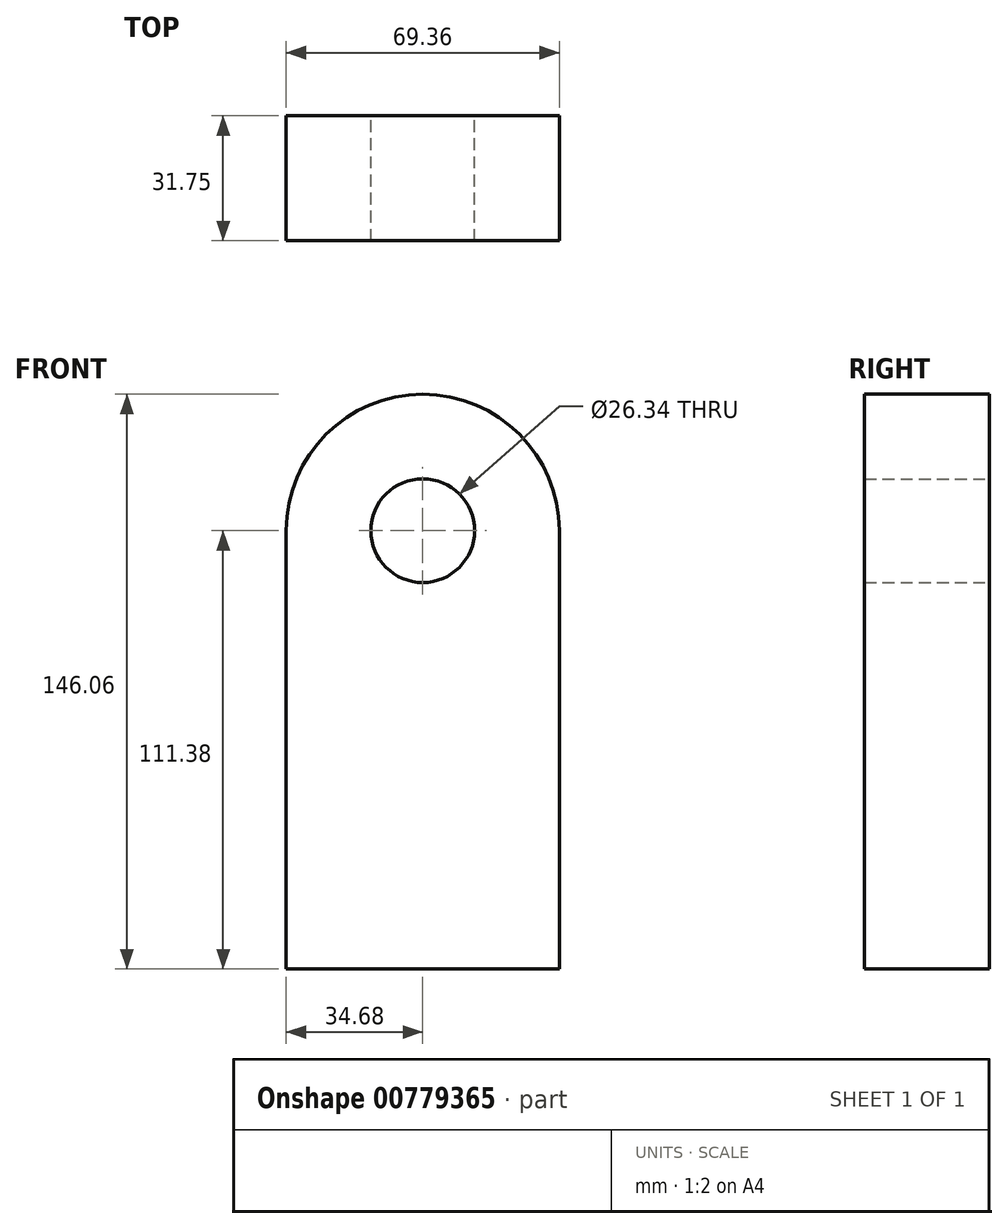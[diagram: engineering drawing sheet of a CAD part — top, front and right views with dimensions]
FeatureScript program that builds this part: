
annotation { "Feature Type Name" : "Feature", "Feature Type Description" : "" }
export const myFeature = defineFeature(function(context is Context, id is Id, definition is map)
    precondition{}
    {
        {
            var Q0;
            Q0=qCreatedBy(makeId("Front.planeOp"),FACE);
            var sketch = newSketch(context, id + "F0", { "sketchPlane" : qUnion([Q0])});
            skLineSegment(sketch, "E0.top", {"start": v(34.68, -55.7) * mm, "end": v(-34.68, -55.7) * mm});
            skLineSegment(sketch, "E0.left", {"start": v(34.68, 55.7) * mm, "end": v(34.68, -55.7) * mm});
            skLineSegment(sketch, "E0.right", {"start": v(-34.68, 55.7) * mm, "end": v(-34.68, -55.7) * mm});
            skPoint(sketch, "E0.middle", {"position": v(0, 0) * mm});
            skArc(sketch, "E1", {"start": v(34.68, 55.7) * mm, "mid": v(0, 90.37) * mm, "end": v(-34.68, 55.7) * mm});
            skCircle(sketch, "E2", {"center": v(0, 55.7) * mm, "radius": 13.17 * mm});
            skArc(sketch, "E3", {"start": v(-34.68, 55.7) * mm, "mid": v(0, 90.37) * mm, "end": v(34.68, 55.7) * mm});
            skSolve(sketch);
        }
        {
            var Q0;
            Q0=makeQuery(id+"F0.imprint","IMPRINT",FACE,{"disambiguationData":[TD([[makeQuery(id+"F0.imprint","IMPRINT",EDGE,{"derivedFrom":sQuery(id+"F0.wireOp",EDGE,"E0.top")}),-1.0]])]});
            extrude(context, id + "F1", {"entities" : qUnion([Q0]), "depth" : 31.75 * mm, "offsetDistance" : 25.4 * mm});
        }
    });
